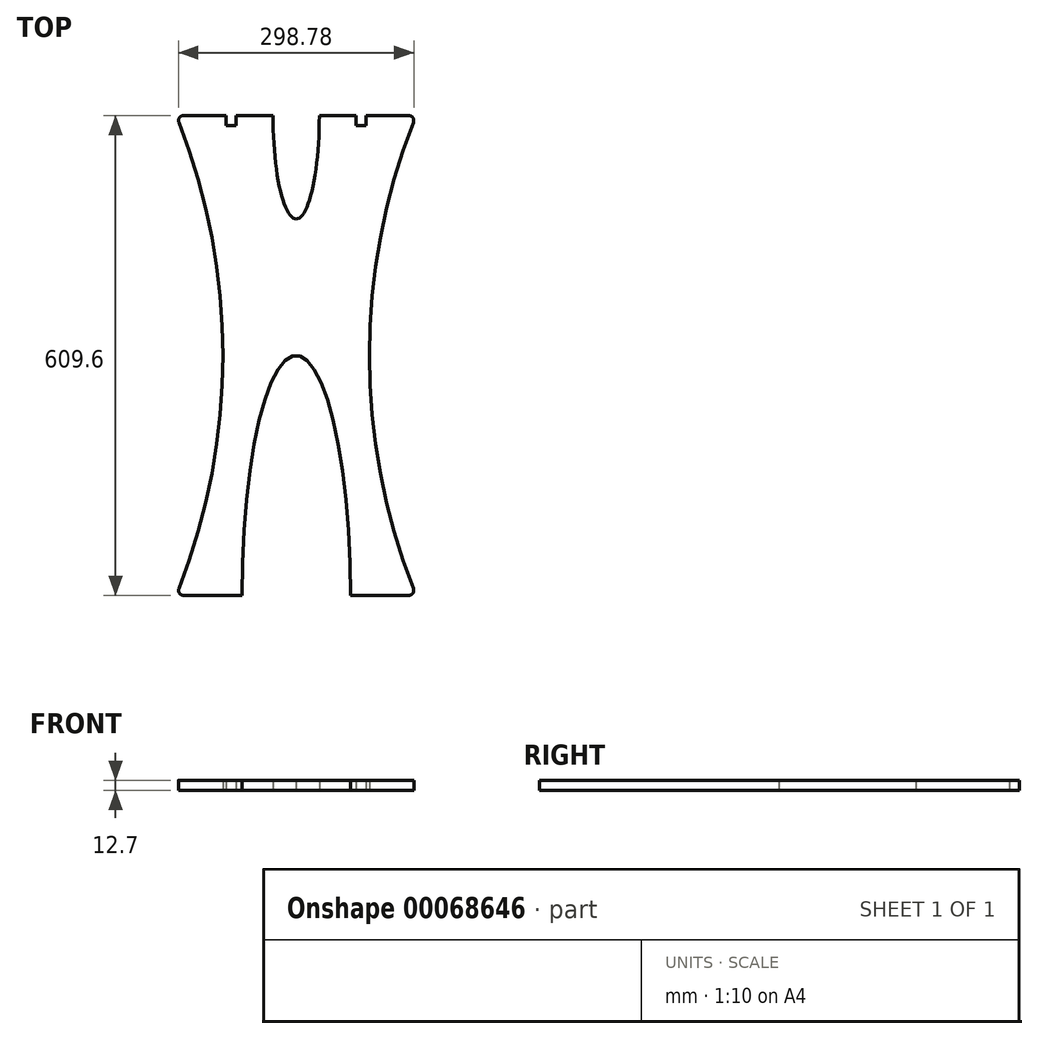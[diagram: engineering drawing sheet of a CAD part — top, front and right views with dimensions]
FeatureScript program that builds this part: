
annotation { "Feature Type Name" : "Feature", "Feature Type Description" : "" }
export const myFeature = defineFeature(function(context is Context, id is Id, definition is map)
    precondition{}
    {
        {
            var Q0;
            Q0=qCreatedBy(makeId("Top.planeOp"),FACE);
            var sketch = newSketch(context, id + "F0", { "sketchPlane" : qUnion([Q0])});
            skLineSegment(sketch, "E0", {"start": v(68.8, 0) * mm, "end": v(143.04, 0) * mm});
            skEllipticalArc(sketch, "E1", {});
            skLineSegment(sketch, "E2", {"start": v(0, 0) * mm, "end": v(0, 667.62) * mm, "construction": true});
            skLineSegment(sketch, "E3", {"start": v(143.04, 609.6) * mm, "end": v(88.9, 609.6) * mm});
            skLineSegment(sketch, "E4.top", {"start": v(76.2, 596.9) * mm, "end": v(88.9, 596.9) * mm});
            skLineSegment(sketch, "E4.left", {"start": v(76.2, 609.6) * mm, "end": v(76.2, 596.9) * mm});
            skLineSegment(sketch, "E4.right", {"start": v(88.9, 609.6) * mm, "end": v(88.9, 596.9) * mm});
            skLineSegment(sketch, "E5.trimOffspring", {"start": v(76.2, 609.6) * mm, "end": v(29.43, 609.6) * mm});
            skArc(sketch, "E6", {"start": v(148.95, 600.94) * mm, "mid": v(93.09, 304.8) * mm, "end": v(148.95, 8.66) * mm});
            skEllipticalArc(sketch, "E7", {});
            skPoint(sketch, "E8.visualSharp", {"position": v(152.4, 0) * mm});
            skArc(sketch, "E8.filletArc", {"start": v(143.04, 0) * mm, "mid": v(148.28, 2.77) * mm, "end": v(148.95, 8.66) * mm});
            skPoint(sketch, "E9.visualSharp", {"position": v(152.4, 609.6) * mm});
            skArc(sketch, "E9.filletArc", {"start": v(148.95, 600.94) * mm, "mid": v(148.28, 606.83) * mm, "end": v(143.04, 609.6) * mm});
            skArc(sketch, "E10.MirrorCS", {"start": v(-143.04, 0) * mm, "mid": v(-148.28, 2.77) * mm, "end": v(-148.95, 8.66) * mm});
            skLineSegment(sketch, "E11.MirrorCS", {"start": v(-88.9, 609.6) * mm, "end": v(-88.9, 596.9) * mm});
            skArc(sketch, "E12.MirrorCS", {"start": v(-148.95, 600.94) * mm, "mid": v(-148.28, 606.83) * mm, "end": v(-143.04, 609.6) * mm});
            skLineSegment(sketch, "E13.MirrorCS", {"start": v(-76.2, 596.9) * mm, "end": v(-88.9, 596.9) * mm});
            skLineSegment(sketch, "E14.MirrorCS", {"start": v(-76.2, 609.6) * mm, "end": v(-76.2, 596.9) * mm});
            skLineSegment(sketch, "E15.MirrorCS", {"start": v(-143.04, 609.6) * mm, "end": v(-88.9, 609.6) * mm});
            skEllipticalArc(sketch, "E16.MirrorCS", {});
            skLineSegment(sketch, "E17.MirrorCS", {"start": v(-76.2, 609.6) * mm, "end": v(-29.43, 609.6) * mm});
            skEllipticalArc(sketch, "E18.MirrorCS", {});
            skLineSegment(sketch, "E19.MirrorCS", {"start": v(-68.8, 0) * mm, "end": v(-143.04, 0) * mm});
            skArc(sketch, "E20.MirrorCS", {"start": v(-148.95, 600.94) * mm, "mid": v(-93.09, 304.8) * mm, "end": v(-148.95, 8.66) * mm});
            skPoint(sketch, "E21.MirrorP", {"position": v(-152.4, 609.6) * mm});
            skPoint(sketch, "E22.MirrorP", {"position": v(-152.4, 0) * mm});
            const initialGuessF0  = {"E1": [0, 0, 0, 1, 0.3048, 0.06880619994088923, 4.71238898038469, 0], "E7": [0, 0.6096302270889282, 0.999999472625248, -0.0010270098470219235, 0.029432131557300123, 0.13147899189327653, 4.7169768011112065, 6.283185307179586], "E16.MirrorCS": [0, 0, 0, 1, 0.3048, 0.06880619994088923, 0, 1.5707963267948966], "E18.MirrorCS": [0, 0.6096302270889282, -0.999999472625248, -0.0010270098470219235, 0.029432131557300123, 0.13147899189327653, 6.283185307179586, 1.5662085060683797]};
            skSetInitialGuess(sketch, initialGuessF0);
            skSolve(sketch);
        }
        {
            var Q0;
            Q0=qSketchRegion(id+"F0",true);
            extrude(context, id + "F1", {"entities" : qUnion([Q0]), "depth" : 12.7 * mm});
        }
    });
